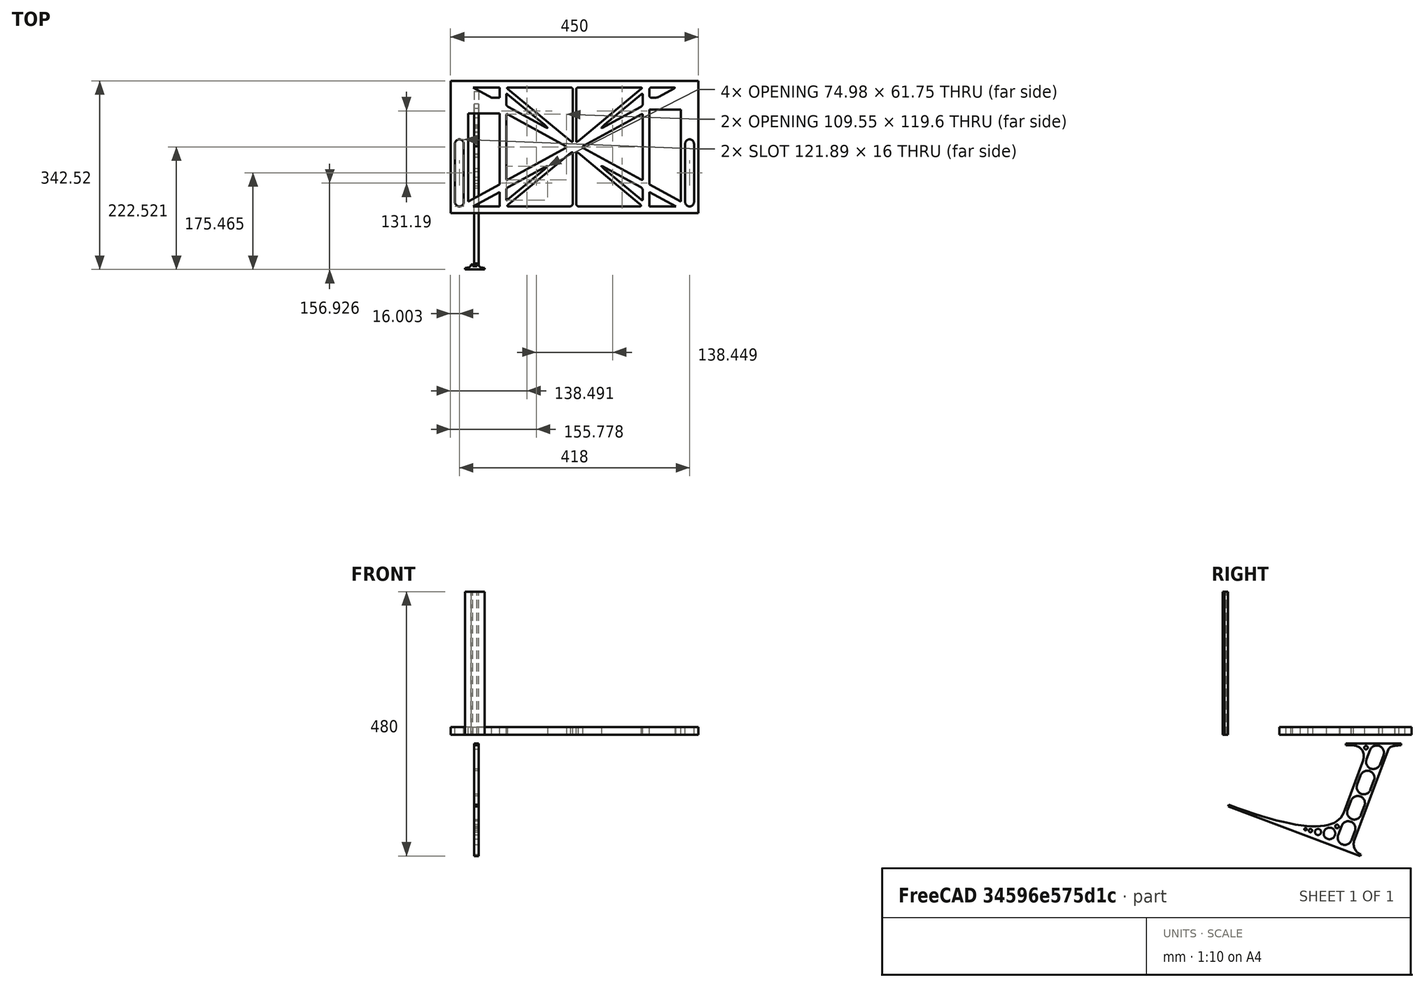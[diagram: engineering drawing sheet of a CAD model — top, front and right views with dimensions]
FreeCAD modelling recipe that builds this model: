
FCSTD DOCUMENT  (FreeCAD 0.19R0.19.2)
Label: laptopStand103
License: All rights reserved
LicenseURL: http://en.wikipedia.org/wiki/All_rights_reserved
objects: Sketcher::SketchObject×3, Part::Extrusion×3
note: 6 computed .brp shape members not serialized (recipe doc carries the construction recipe); baked Part::Feature solids carry a one-line shape summary decoded from their .brp

FEATURE [Sketcher::SketchObject] Sketch
  FullyConstrained = false
  sketch-geometry (282):
    g0: LineSegment StartX=-10.9272 StartY=-82.7794 StartZ=0 EndX=46.0728 EndY=-51.4823 EndZ=0
    g1: LineSegment StartX=366.073 StartY=-91.7794 StartZ=0 EndX=318.073 EndY=-65.424 EndZ=0
    g2: LineSegment StartX=-10.9272 StartY=77.3346 StartZ=0 EndX=-10.9272 EndY=-82.7794 EndZ=0
    g3: LineSegment StartX=375.073 StartY=-82.7896 StartZ=0 EndX=375.073 EndY=83.9235 EndZ=0
    g4: LineSegment StartX=-1.92719 StartY=-91.7794 StartZ=0 EndX=46.0728 EndY=-91.7794 EndZ=0
    g5: LineSegment StartX=318.073 StartY=83.9235 StartZ=0 EndX=318.073 EndY=-51.4823 EndZ=0
    g6: LineSegment StartX=318.073 StartY=-51.4823 StartZ=0 EndX=375.073 EndY=-82.7794 EndZ=0
    g7: LineSegment StartX=318.073 StartY=-65.424 StartZ=0 EndX=318.073 EndY=-91.7794 EndZ=0
    g8: LineSegment StartX=318.073 StartY=-91.7794 StartZ=0 EndX=366.073 EndY=-91.7794 EndZ=0
    g9: LineSegment StartX=46.0728 StartY=-65.424 StartZ=0 EndX=-1.92719 EndY=-91.7794 EndZ=0
    g10: LineSegment StartX=46.0728 StartY=-65.424 StartZ=0 EndX=46.0728 EndY=-91.7794 EndZ=0
    g11: LineSegment StartX=46.0728 StartY=77.3346 StartZ=0 EndX=46.0728 EndY=-51.4823 EndZ=0
    g12: LineSegment StartX=-42.9272 StartY=136.221 StartZ=0 EndX=-42.9272 EndY=-103.779 EndZ=0
    g13: LineSegment StartX=407.073 StartY=136.221 StartZ=0 EndX=407.073 EndY=-103.779 EndZ=0
    g14: ArcOfCircle CenterX=-26.9272 CenterY=22.1087 CenterZ=0 NormalX=0 NormalY=0 NormalZ=1 AngleXU=0 Radius=8 StartAngle=1e-16 EndAngle=3.14159
    g15: ArcOfCircle CenterX=-26.9272 CenterY=-83.7794 CenterZ=0 NormalX=0 NormalY=0 NormalZ=1 AngleXU=0 Radius=8 StartAngle=3.14159 EndAngle=6.28319
    g16: LineSegment StartX=-34.9272 StartY=22.1087 StartZ=0 EndX=-34.9272 EndY=-83.7794 EndZ=0
    g17: LineSegment StartX=-18.9272 StartY=22.1087 StartZ=0 EndX=-18.9272 EndY=-83.7794 EndZ=0
    g18: ArcOfCircle CenterX=391.073 CenterY=22.1087 CenterZ=0 NormalX=0 NormalY=0 NormalZ=1 AngleXU=0 Radius=8 StartAngle=-4.4e-15 EndAngle=3.14159
    g19: LineSegment StartX=399.073 StartY=22.1087 StartZ=0 EndX=399.073 EndY=-83.7794 EndZ=0
    g20: LineSegment StartX=383.073 StartY=22.1087 StartZ=0 EndX=383.073 EndY=-83.7794 EndZ=0
    g21: ArcOfCircle CenterX=391.073 CenterY=-83.7794 CenterZ=0 NormalX=0 NormalY=0 NormalZ=1 AngleXU=0 Radius=8 StartAngle=3.14159 EndAngle=6.28319
    g22: Circle CenterX=175.022 CenterY=27.0628 CenterZ=0 NormalX=0 NormalY=0 NormalZ=1 AngleXU=0 Radius=1
    g23: Circle CenterX=179.022 CenterY=24.8665 CenterZ=0 NormalX=0 NormalY=0 NormalZ=1 AngleXU=0 Radius=1
    g24: Circle CenterX=179.022 CenterY=27.0628 CenterZ=0 NormalX=0 NormalY=0 NormalZ=1 AngleXU=0 Radius=1
    g25: BSplineCurve PolesCount=3 KnotsCount=2 Degree=2 IsPeriodic=0
    g26: GeomPoint X=175.022 Y=27.0628 Z=0
    g27: GeomPoint X=179.022 Y=27.0628 Z=0
    g28: Circle CenterX=189.124 CenterY=27.0628 CenterZ=0 NormalX=0 NormalY=0 NormalZ=1 AngleXU=0 Radius=1
    g29: Circle CenterX=185.124 CenterY=24.8665 CenterZ=0 NormalX=0 NormalY=0 NormalZ=1 AngleXU=0 Radius=1
    g30: Circle CenterX=185.124 CenterY=27.0628 CenterZ=0 NormalX=0 NormalY=0 NormalZ=1 AngleXU=0 Radius=1
    g31: BSplineCurve PolesCount=3 KnotsCount=2 Degree=2 IsPeriodic=0
    g32: GeomPoint X=189.124 Y=27.0628 Z=0
    g33: GeomPoint X=185.124 Y=27.0628 Z=0
    g34: Circle CenterX=175.022 CenterY=5.37834 CenterZ=0 NormalX=0 NormalY=0 NormalZ=1 AngleXU=0 Radius=1
    g35: Circle CenterX=179.022 CenterY=7.57463 CenterZ=0 NormalX=0 NormalY=0 NormalZ=1 AngleXU=0 Radius=1
    g36: Circle CenterX=179.022 CenterY=5.34704 CenterZ=0 NormalX=0 NormalY=0 NormalZ=1 AngleXU=0 Radius=1
    g37: BSplineCurve PolesCount=3 KnotsCount=2 Degree=2 IsPeriodic=0
    g38: GeomPoint X=175.022 Y=5.37834 Z=0
    g39: GeomPoint X=179.022 Y=5.34704 Z=0
    g40: Circle CenterX=189.124 CenterY=5.37834 CenterZ=0 NormalX=0 NormalY=0 NormalZ=1 AngleXU=0 Radius=1
    g41: Circle CenterX=185.124 CenterY=7.57463 CenterZ=0 NormalX=0 NormalY=0 NormalZ=1 AngleXU=0 Radius=1
    g42: Circle CenterX=185.124 CenterY=5.34704 CenterZ=0 NormalX=0 NormalY=0 NormalZ=1 AngleXU=0 Radius=1
    g43: BSplineCurve PolesCount=3 KnotsCount=2 Degree=2 IsPeriodic=0
    g44: GeomPoint X=189.124 Y=5.37834 Z=0
    g45: GeomPoint X=185.124 Y=5.34704 Z=0
    g46: Circle CenterX=165.871 CenterY=18.1458 CenterZ=0 NormalX=0 NormalY=0 NormalZ=1 AngleXU=0 Radius=1
    g47: Circle CenterX=169.377 CenterY=16.2206 CenterZ=0 NormalX=0 NormalY=0 NormalZ=1 AngleXU=0 Radius=1
    g48: Circle CenterX=165.871 CenterY=14.2954 CenterZ=0 NormalX=0 NormalY=0 NormalZ=1 AngleXU=0 Radius=1
    g49: BSplineCurve PolesCount=3 KnotsCount=2 Degree=2 IsPeriodic=0
    g50: GeomPoint X=165.871 Y=18.1458 Z=0
    g51: GeomPoint X=165.871 Y=14.2954 Z=0
    g52: Circle CenterX=198.275 CenterY=18.1458 CenterZ=0 NormalX=0 NormalY=0 NormalZ=1 AngleXU=0 Radius=1
    g53: Circle CenterX=194.768 CenterY=16.2206 CenterZ=0 NormalX=0 NormalY=0 NormalZ=1 AngleXU=0 Radius=1
    g54: Circle CenterX=198.275 CenterY=14.2954 CenterZ=0 NormalX=0 NormalY=0 NormalZ=1 AngleXU=0 Radius=1
    g55: BSplineCurve PolesCount=3 KnotsCount=2 Degree=2 IsPeriodic=0
    g56: GeomPoint X=198.275 Y=18.1458 Z=0
    g57: GeomPoint X=198.275 Y=14.2954 Z=0
    g58: LineSegment StartX=407.073 StartY=-103.779 StartZ=0 EndX=-42.9272 EndY=-103.779 EndZ=0
    g59: LineSegment StartX=407.073 StartY=136.221 StartZ=0 EndX=-42.9272 EndY=136.221 EndZ=0
    g60: LineSegment StartX=46.0728 StartY=77.3346 StartZ=0 EndX=-10.9272 EndY=77.3346 EndZ=0
    g61: LineSegment StartX=46.0728 StartY=105.865 StartZ=0 EndX=31.5028 EndY=105.865 EndZ=0
    g62: LineSegment StartX=46.0728 StartY=124.221 StartZ=0 EndX=46.0728 EndY=105.865 EndZ=0
    g63: LineSegment StartX=-1.92719 StartY=124.221 StartZ=0 EndX=31.5028 EndY=105.865 EndZ=0
    g64: LineSegment StartX=46.0728 StartY=124.221 StartZ=0 EndX=-1.92719 EndY=124.221 EndZ=0
    g65: LineSegment StartX=318.073 StartY=83.9235 StartZ=0 EndX=375.073 EndY=83.9235 EndZ=0
    g66: Circle CenterX=125.607 CenterY=54.1951 CenterZ=0 NormalX=0 NormalY=0 NormalZ=1 AngleXU=0 Radius=1
    g67: Circle CenterX=139.632 CenterY=46.4944 CenterZ=0 NormalX=0 NormalY=0 NormalZ=1 AngleXU=0 Radius=1
    g68: Circle CenterX=127.326 CenterY=56.7187 CenterZ=0 NormalX=0 NormalY=0 NormalZ=1 AngleXU=0 Radius=1
    g69: BSplineCurve PolesCount=3 KnotsCount=2 Degree=2 IsPeriodic=0
    g70: GeomPoint X=125.607 Y=54.1951 Z=0
    g71: GeomPoint X=127.326 Y=56.7187 Z=0
    g72: Circle CenterX=236.821 CenterY=56.7187 CenterZ=0 NormalX=0 NormalY=0 NormalZ=1 AngleXU=0 Radius=1
    g73: Circle CenterX=224.513 CenterY=46.4944 CenterZ=0 NormalX=0 NormalY=0 NormalZ=1 AngleXU=0 Radius=1
    g74: Circle CenterX=238.538 CenterY=54.1951 CenterZ=0 NormalX=0 NormalY=0 NormalZ=1 AngleXU=0 Radius=1
    g75: BSplineCurve PolesCount=3 KnotsCount=2 Degree=2 IsPeriodic=0
    g76: GeomPoint X=236.821 Y=56.7187 Z=0
    g77: GeomPoint X=238.538 Y=54.1951 Z=0
    g78: Circle CenterX=238.538 CenterY=-21.7539 CenterZ=0 NormalX=0 NormalY=0 NormalZ=1 AngleXU=0 Radius=1
    g79: Circle CenterX=224.513 CenterY=-14.0532 CenterZ=0 NormalX=0 NormalY=0 NormalZ=1 AngleXU=0 Radius=1
    g80: Circle CenterX=236.821 CenterY=-24.2775 CenterZ=0 NormalX=0 NormalY=0 NormalZ=1 AngleXU=0 Radius=1
    g81: BSplineCurve PolesCount=3 KnotsCount=2 Degree=2 IsPeriodic=0
    g82: GeomPoint X=238.538 Y=-21.7539 Z=0
    g83: GeomPoint X=236.821 Y=-24.2775 Z=0
    g84: Circle CenterX=125.607 CenterY=-21.7539 CenterZ=0 NormalX=0 NormalY=0 NormalZ=1 AngleXU=0 Radius=1
    g85: Circle CenterX=139.632 CenterY=-14.0532 CenterZ=0 NormalX=0 NormalY=0 NormalZ=1 AngleXU=0 Radius=1
    g86: Circle CenterX=127.325 CenterY=-24.2775 CenterZ=0 NormalX=0 NormalY=0 NormalZ=1 AngleXU=0 Radius=1
    g87: BSplineCurve PolesCount=3 KnotsCount=2 Degree=2 IsPeriodic=0
    g88: GeomPoint X=125.607 Y=-21.7539 Z=0
    g89: GeomPoint X=127.325 Y=-24.2775 Z=0
    g90: Circle CenterX=302.996 CenterY=111.695 CenterZ=0 NormalX=0 NormalY=0 NormalZ=1 AngleXU=0 Radius=1
    g91: Circle CenterX=306.073 CenterY=114.251 CenterZ=0 NormalX=0 NormalY=0 NormalZ=1 AngleXU=0 Radius=1
    g92: Circle CenterX=306.073 CenterY=110.251 CenterZ=0 NormalX=0 NormalY=0 NormalZ=1 AngleXU=0 Radius=1
    g93: BSplineCurve PolesCount=3 KnotsCount=2 Degree=2 IsPeriodic=0
    g94: GeomPoint X=302.996 Y=111.695 Z=0
    g95: GeomPoint X=306.073 Y=110.251 Z=0
    g96: Circle CenterX=306.073 CenterY=95.2763 CenterZ=0 NormalX=0 NormalY=0 NormalZ=1 AngleXU=0 Radius=1
    g97: Circle CenterX=306.073 CenterY=91.2763 CenterZ=0 NormalX=0 NormalY=0 NormalZ=1 AngleXU=0 Radius=1
    g98: Circle CenterX=302.567 CenterY=89.3511 CenterZ=0 NormalX=0 NormalY=0 NormalZ=1 AngleXU=0 Radius=1
    g99: BSplineCurve PolesCount=3 KnotsCount=2 Degree=2 IsPeriodic=0
    g100: GeomPoint X=306.073 Y=95.2763 Z=0
    g101: GeomPoint X=302.567 Y=89.3511 Z=0
    g102: LineSegment StartX=306.073 StartY=110.251 StartZ=0 EndX=306.073 EndY=95.2763 EndZ=0
    g103: LineSegment StartX=302.996 StartY=111.695 StartZ=0 EndX=236.821 EndY=56.7187 EndZ=0
    g104: LineSegment StartX=238.538 StartY=54.1951 StartZ=0 EndX=302.567 EndY=89.3511 EndZ=0
    g105: Circle CenterX=61.1496 CenterY=111.695 CenterZ=0 NormalX=0 NormalY=0 NormalZ=1 AngleXU=0 Radius=1
    g106: Circle CenterX=58.0728 CenterY=114.251 CenterZ=0 NormalX=0 NormalY=0 NormalZ=1 AngleXU=0 Radius=1
    g107: Circle CenterX=58.0728 CenterY=110.251 CenterZ=0 NormalX=0 NormalY=0 NormalZ=1 AngleXU=0 Radius=1
    g108: BSplineCurve PolesCount=3 KnotsCount=2 Degree=2 IsPeriodic=0
    g109: GeomPoint X=61.1496 Y=111.695 Z=0
    g110: GeomPoint X=58.0728 Y=110.251 Z=0
    g111: Circle CenterX=61.5791 CenterY=89.3511 CenterZ=0 NormalX=0 NormalY=0 NormalZ=1 AngleXU=0 Radius=1
    g112: Circle CenterX=58.0728 CenterY=91.2763 CenterZ=0 NormalX=0 NormalY=0 NormalZ=1 AngleXU=0 Radius=1
    g113: Circle CenterX=58.0728 CenterY=95.2763 CenterZ=0 NormalX=0 NormalY=0 NormalZ=1 AngleXU=0 Radius=1
    g114: BSplineCurve PolesCount=3 KnotsCount=2 Degree=2 IsPeriodic=0
    g115: GeomPoint X=61.5791 Y=89.3511 Z=0
    g116: GeomPoint X=58.0728 Y=95.2763 Z=0
    g117: LineSegment StartX=58.0728 StartY=110.251 StartZ=0 EndX=58.0728 EndY=95.2763 EndZ=0
    g118: LineSegment StartX=61.1496 StartY=111.695 StartZ=0 EndX=127.326 EndY=56.7187 EndZ=0
    g119: LineSegment StartX=125.607 StartY=54.1951 StartZ=0 EndX=61.5791 EndY=89.3511 EndZ=0
    g120: Circle CenterX=61.5791 CenterY=-56.9099 CenterZ=0 NormalX=0 NormalY=0 NormalZ=1 AngleXU=0 Radius=1
    g121: Circle CenterX=58.0728 CenterY=-58.8351 CenterZ=0 NormalX=0 NormalY=0 NormalZ=1 AngleXU=0 Radius=1
    g122: Circle CenterX=58.0728 CenterY=-62.8351 CenterZ=0 NormalX=0 NormalY=0 NormalZ=1 AngleXU=0 Radius=1
    g123: BSplineCurve PolesCount=3 KnotsCount=2 Degree=2 IsPeriodic=0
    g124: GeomPoint X=61.5791 Y=-56.9099 Z=0
    g125: GeomPoint X=58.0728 Y=-62.8351 Z=0
    g126: Circle CenterX=58.0728 CenterY=-77.8102 CenterZ=0 NormalX=0 NormalY=0 NormalZ=1 AngleXU=0 Radius=1
    g127: Circle CenterX=58.0728 CenterY=-81.8102 CenterZ=0 NormalX=0 NormalY=0 NormalZ=1 AngleXU=0 Radius=1
    g128: Circle CenterX=61.1496 CenterY=-79.2541 CenterZ=0 NormalX=0 NormalY=0 NormalZ=1 AngleXU=0 Radius=1
    g129: BSplineCurve PolesCount=3 KnotsCount=2 Degree=2 IsPeriodic=0
    g130: GeomPoint X=58.0728 Y=-77.8102 Z=0
    g131: GeomPoint X=61.1496 Y=-79.2541 Z=0
    g132: LineSegment StartX=58.0728 StartY=-62.8351 StartZ=0 EndX=58.0728 EndY=-77.8102 EndZ=0
    g133: LineSegment StartX=61.1496 StartY=-79.2541 StartZ=0 EndX=127.325 EndY=-24.2775 EndZ=0
    g134: LineSegment StartX=125.607 StartY=-21.7539 StartZ=0 EndX=61.5791 EndY=-56.9099 EndZ=0
    g135: Circle CenterX=302.567 CenterY=-56.9099 CenterZ=0 NormalX=0 NormalY=0 NormalZ=1 AngleXU=0 Radius=1
    g136: Circle CenterX=306.073 CenterY=-58.8351 CenterZ=0 NormalX=0 NormalY=0 NormalZ=1 AngleXU=0 Radius=1
    g137: Circle CenterX=306.073 CenterY=-62.8351 CenterZ=0 NormalX=0 NormalY=0 NormalZ=1 AngleXU=0 Radius=1
    g138: BSplineCurve PolesCount=3 KnotsCount=2 Degree=2 IsPeriodic=0
    g139: GeomPoint X=302.567 Y=-56.9099 Z=0
    g140: GeomPoint X=306.073 Y=-62.8351 Z=0
    g141: Circle CenterX=302.996 CenterY=-79.2541 CenterZ=0 NormalX=0 NormalY=0 NormalZ=1 AngleXU=0 Radius=1
    g142: Circle CenterX=306.073 CenterY=-81.8102 CenterZ=0 NormalX=0 NormalY=0 NormalZ=1 AngleXU=0 Radius=1
    g143: Circle CenterX=306.073 CenterY=-77.8102 CenterZ=0 NormalX=0 NormalY=0 NormalZ=1 AngleXU=0 Radius=1
    g144: BSplineCurve PolesCount=3 KnotsCount=2 Degree=2 IsPeriodic=0
    g145: GeomPoint X=302.996 Y=-79.2541 Z=0
    g146: GeomPoint X=306.073 Y=-77.8102 Z=0
    g147: LineSegment StartX=306.073 StartY=-62.8351 StartZ=0 EndX=306.073 EndY=-77.8102 EndZ=0
    g148: LineSegment StartX=302.996 StartY=-79.2541 StartZ=0 EndX=236.821 EndY=-24.2775 EndZ=0
    g149: LineSegment StartX=238.538 StartY=-21.7539 StartZ=0 EndX=302.567 EndY=-56.9099 EndZ=0
    g150: Circle CenterX=61.6457 CenterY=-88.8112 CenterZ=0 NormalX=0 NormalY=0 NormalZ=1 AngleXU=0 Radius=1
    g151: Circle CenterX=58.0728 CenterY=-91.7794 CenterZ=0 NormalX=0 NormalY=0 NormalZ=1 AngleXU=0 Radius=1
    g152: Circle CenterX=63.9135 CenterY=-91.7794 CenterZ=0 NormalX=0 NormalY=0 NormalZ=1 AngleXU=0 Radius=1
    g153: BSplineCurve PolesCount=3 KnotsCount=2 Degree=2 IsPeriodic=0
    g154: GeomPoint X=61.6457 Y=-88.8112 Z=0
    g155: GeomPoint X=63.9135 Y=-91.7794 Z=0
    g156: Circle CenterX=179.022 CenterY=-85.8163 CenterZ=0 NormalX=0 NormalY=0 NormalZ=1 AngleXU=0 Radius=1
    g157: Circle CenterX=179.022 CenterY=-91.7794 CenterZ=0 NormalX=0 NormalY=0 NormalZ=1 AngleXU=0 Radius=1
    g158: Circle CenterX=171.895 CenterY=-91.7794 CenterZ=0 NormalX=0 NormalY=0 NormalZ=1 AngleXU=0 Radius=1
    g159: BSplineCurve PolesCount=3 KnotsCount=2 Degree=2 IsPeriodic=0
    g160: GeomPoint X=179.022 Y=-85.8163 Z=0
    g161: GeomPoint X=171.895 Y=-91.7794 Z=0
    g162: Circle CenterX=185.124 CenterY=-86.2028 CenterZ=0 NormalX=0 NormalY=0 NormalZ=1 AngleXU=0 Radius=1
    g163: Circle CenterX=185.124 CenterY=-91.7794 CenterZ=0 NormalX=0 NormalY=0 NormalZ=1 AngleXU=0 Radius=1
    g164: Circle CenterX=191.747 CenterY=-91.7794 CenterZ=0 NormalX=0 NormalY=0 NormalZ=1 AngleXU=0 Radius=1
    g165: BSplineCurve PolesCount=3 KnotsCount=2 Degree=2 IsPeriodic=0
    g166: GeomPoint X=185.124 Y=-86.2028 Z=0
    g167: GeomPoint X=191.747 Y=-91.7794 Z=0
    g168: Circle CenterX=299.888 CenterY=-86.6413 CenterZ=0 NormalX=0 NormalY=0 NormalZ=1 AngleXU=0 Radius=1
    g169: Circle CenterX=306.073 CenterY=-91.7794 CenterZ=0 NormalX=0 NormalY=0 NormalZ=1 AngleXU=0 Radius=1
    g170: Circle CenterX=298.776 CenterY=-91.7794 CenterZ=0 NormalX=0 NormalY=0 NormalZ=1 AngleXU=0 Radius=1
    g171: BSplineCurve PolesCount=3 KnotsCount=2 Degree=2 IsPeriodic=0
    g172: GeomPoint X=299.888 Y=-86.6413 Z=0
    g173: GeomPoint X=298.776 Y=-91.7794 Z=0
    g174: LineSegment StartX=189.124 StartY=5.37834 StartZ=0 EndX=299.888 EndY=-86.6413 EndZ=0
    g175: LineSegment StartX=298.776 StartY=-91.7794 StartZ=0 EndX=191.747 EndY=-91.7794 EndZ=0
    g176: LineSegment StartX=185.124 StartY=-86.2028 StartZ=0 EndX=185.124 EndY=5.34704 EndZ=0
    g177: LineSegment StartX=179.022 StartY=5.34704 StartZ=0 EndX=179.022 EndY=-85.8163 EndZ=0
    g178: LineSegment StartX=171.895 StartY=-91.7794 StartZ=0 EndX=63.9135 EndY=-91.7794 EndZ=0
    g179: LineSegment StartX=61.6457 StartY=-88.8112 StartZ=0 EndX=175.022 EndY=5.37834 EndZ=0
    g180: Circle CenterX=302.073 CenterY=124.221 CenterZ=0 NormalX=0 NormalY=0 NormalZ=1 AngleXU=0 Radius=1
    g181: Circle CenterX=306.073 CenterY=124.221 CenterZ=0 NormalX=0 NormalY=0 NormalZ=1 AngleXU=0 Radius=1
    g182: Circle CenterX=302.996 CenterY=121.665 CenterZ=0 NormalX=0 NormalY=0 NormalZ=1 AngleXU=0 Radius=1
    g183: BSplineCurve PolesCount=3 KnotsCount=2 Degree=2 IsPeriodic=0
    g184: GeomPoint X=302.073 Y=124.221 Z=0
    g185: GeomPoint X=302.996 Y=121.665 Z=0
    g186: Circle CenterX=189.124 CenterY=124.221 CenterZ=0 NormalX=0 NormalY=0 NormalZ=1 AngleXU=0 Radius=1
    g187: Circle CenterX=185.124 CenterY=124.221 CenterZ=0 NormalX=0 NormalY=0 NormalZ=1 AngleXU=0 Radius=1
    g188: Circle CenterX=185.124 CenterY=120.221 CenterZ=0 NormalX=0 NormalY=0 NormalZ=1 AngleXU=0 Radius=1
    g189: BSplineCurve PolesCount=3 KnotsCount=2 Degree=2 IsPeriodic=0
    g190: GeomPoint X=189.124 Y=124.221 Z=0
    g191: GeomPoint X=185.124 Y=120.221 Z=0
    g192: Circle CenterX=175.022 CenterY=124.221 CenterZ=0 NormalX=0 NormalY=0 NormalZ=1 AngleXU=0 Radius=1
    g193: Circle CenterX=179.022 CenterY=124.221 CenterZ=0 NormalX=0 NormalY=0 NormalZ=1 AngleXU=0 Radius=1
    g194: Circle CenterX=179.022 CenterY=120.221 CenterZ=0 NormalX=0 NormalY=0 NormalZ=1 AngleXU=0 Radius=1
    g195: BSplineCurve PolesCount=3 KnotsCount=2 Degree=2 IsPeriodic=0
    g196: GeomPoint X=175.022 Y=124.221 Z=0
    g197: GeomPoint X=179.022 Y=120.221 Z=0
    g198: Circle CenterX=62.0728 CenterY=124.221 CenterZ=0 NormalX=0 NormalY=0 NormalZ=1 AngleXU=0 Radius=1
    g199: Circle CenterX=58.0728 CenterY=124.221 CenterZ=0 NormalX=0 NormalY=0 NormalZ=1 AngleXU=0 Radius=1
    g200: Circle CenterX=61.1496 CenterY=121.665 CenterZ=0 NormalX=0 NormalY=0 NormalZ=1 AngleXU=0 Radius=1
    g201: BSplineCurve PolesCount=3 KnotsCount=2 Degree=2 IsPeriodic=0
    g202: GeomPoint X=62.0728 Y=124.221 Z=0
    g203: GeomPoint X=61.1496 Y=121.665 Z=0
    g204: LineSegment StartX=62.0728 StartY=124.221 StartZ=0 EndX=175.022 EndY=124.221 EndZ=0
    g205: LineSegment StartX=179.022 StartY=120.221 StartZ=0 EndX=179.022 EndY=27.0628 EndZ=0
    g206: LineSegment StartX=185.124 StartY=27.0628 StartZ=0 EndX=185.124 EndY=120.221 EndZ=0
    g207: LineSegment StartX=189.124 StartY=124.221 StartZ=0 EndX=302.073 EndY=124.221 EndZ=0
    g208: LineSegment StartX=302.996 StartY=121.665 StartZ=0 EndX=189.124 EndY=27.0628 EndZ=0
    g209: LineSegment StartX=175.022 StartY=27.0628 StartZ=0 EndX=61.1496 EndY=121.665 EndZ=0
    g210: Circle CenterX=61.5791 CenterY=75.4095 CenterZ=0 NormalX=0 NormalY=0 NormalZ=1 AngleXU=0 Radius=1
    g211: Circle CenterX=58.0728 CenterY=77.3346 CenterZ=0 NormalX=0 NormalY=0 NormalZ=1 AngleXU=0 Radius=1
    g212: Circle CenterX=58.0728 CenterY=73.3346 CenterZ=0 NormalX=0 NormalY=0 NormalZ=1 AngleXU=0 Radius=1
    g213: BSplineCurve PolesCount=3 KnotsCount=2 Degree=2 IsPeriodic=0
    g214: GeomPoint X=61.5791 Y=75.4095 Z=0
    g215: GeomPoint X=58.0728 Y=73.3346 Z=0
    g216: Circle CenterX=58.0728 CenterY=-40.8935 CenterZ=0 NormalX=0 NormalY=0 NormalZ=1 AngleXU=0 Radius=1
    g217: Circle CenterX=58.0728 CenterY=-44.8935 CenterZ=0 NormalX=0 NormalY=0 NormalZ=1 AngleXU=0 Radius=1
    g218: Circle CenterX=61.5791 CenterY=-42.9683 CenterZ=0 NormalX=0 NormalY=0 NormalZ=1 AngleXU=0 Radius=1
    g219: BSplineCurve PolesCount=3 KnotsCount=2 Degree=2 IsPeriodic=0
    g220: GeomPoint X=58.0728 Y=-40.8935 Z=0
    g221: GeomPoint X=61.5791 Y=-42.9683 Z=0
    g222: LineSegment StartX=61.5791 StartY=-42.9683 StartZ=0 EndX=165.871 EndY=14.2954 EndZ=0
    g223: LineSegment StartX=165.871 StartY=18.1458 StartZ=0 EndX=61.5791 EndY=75.4095 EndZ=0
    g224: LineSegment StartX=58.0728 StartY=73.3346 StartZ=0 EndX=58.0728 EndY=-40.8935 EndZ=0
    g225: Circle CenterX=302.567 CenterY=-42.9683 CenterZ=0 NormalX=0 NormalY=0 NormalZ=1 AngleXU=0 Radius=1
    g226: Circle CenterX=306.073 CenterY=-44.8935 CenterZ=0 NormalX=0 NormalY=0 NormalZ=1 AngleXU=0 Radius=1
    g227: Circle CenterX=306.073 CenterY=-40.8935 CenterZ=0 NormalX=0 NormalY=0 NormalZ=1 AngleXU=0 Radius=1
    g228: BSplineCurve PolesCount=3 KnotsCount=2 Degree=2 IsPeriodic=0
    g229: GeomPoint X=302.567 Y=-42.9683 Z=0
    g230: GeomPoint X=306.073 Y=-40.8935 Z=0
    g231: Circle CenterX=306.073 CenterY=73.3346 CenterZ=0 NormalX=0 NormalY=0 NormalZ=1 AngleXU=0 Radius=1
    g232: Circle CenterX=306.073 CenterY=77.3346 CenterZ=0 NormalX=0 NormalY=0 NormalZ=1 AngleXU=0 Radius=1
    g233: Circle CenterX=302.567 CenterY=75.4095 CenterZ=0 NormalX=0 NormalY=0 NormalZ=1 AngleXU=0 Radius=1
    g234: BSplineCurve PolesCount=3 KnotsCount=2 Degree=2 IsPeriodic=0
    g235: GeomPoint X=306.073 Y=73.3346 Z=0
    g236: GeomPoint X=302.567 Y=75.4095 Z=0
    g237: LineSegment StartX=302.567 StartY=-42.9683 StartZ=0 EndX=198.275 EndY=14.2954 EndZ=0
    g238: LineSegment StartX=198.275 StartY=18.1458 StartZ=0 EndX=302.567 EndY=75.4095 EndZ=0
    g239: LineSegment StartX=306.073 StartY=73.3346 StartZ=0 EndX=306.073 EndY=-40.8935 EndZ=0
    g240: LineSegment StartX=322.073 StartY=105.865 StartZ=0 EndX=328.643 EndY=105.865 EndZ=0
    g241: LineSegment StartX=318.073 StartY=120.221 StartZ=0 EndX=318.073 EndY=109.865 EndZ=0
    g242: LineSegment StartX=336.157 StartY=107.779 StartZ=0 EndX=362.567 EndY=122.294 EndZ=0
    g243: Circle CenterX=362.073 CenterY=124.221 CenterZ=0 NormalX=0 NormalY=0 NormalZ=1 AngleXU=0 Radius=1
    g244: Circle CenterX=366.073 CenterY=124.221 CenterZ=0 NormalX=0 NormalY=0 NormalZ=1 AngleXU=0 Radius=1
    g245: Circle CenterX=362.567 CenterY=122.294 CenterZ=0 NormalX=0 NormalY=0 NormalZ=1 AngleXU=0 Radius=1
    g246: BSplineCurve PolesCount=3 KnotsCount=2 Degree=2 IsPeriodic=0
    g247: GeomPoint X=362.073 Y=124.221 Z=0
    g248: GeomPoint X=362.567 Y=122.294 Z=0
    g249: Circle CenterX=322.073 CenterY=124.221 CenterZ=0 NormalX=0 NormalY=0 NormalZ=1 AngleXU=0 Radius=1
    g250: Circle CenterX=318.073 CenterY=124.221 CenterZ=0 NormalX=0 NormalY=0 NormalZ=1 AngleXU=0 Radius=1
    g251: Circle CenterX=318.073 CenterY=120.221 CenterZ=0 NormalX=0 NormalY=0 NormalZ=1 AngleXU=0 Radius=1
    g252: BSplineCurve PolesCount=3 KnotsCount=2 Degree=2 IsPeriodic=0
    g253: GeomPoint X=322.073 Y=124.221 Z=0
    g254: GeomPoint X=318.073 Y=120.221 Z=0
    g255: Circle CenterX=322.073 CenterY=105.865 CenterZ=0 NormalX=0 NormalY=0 NormalZ=1 AngleXU=0 Radius=1
    g256: Circle CenterX=318.073 CenterY=105.865 CenterZ=0 NormalX=0 NormalY=0 NormalZ=1 AngleXU=0 Radius=1
    g257: Circle CenterX=318.073 CenterY=109.865 CenterZ=0 NormalX=0 NormalY=0 NormalZ=1 AngleXU=0 Radius=1
    g258: BSplineCurve PolesCount=3 KnotsCount=2 Degree=2 IsPeriodic=0
    g259: GeomPoint X=322.073 Y=105.865 Z=0
    g260: GeomPoint X=318.073 Y=109.865 Z=0
    g261: Circle CenterX=336.157 CenterY=107.779 CenterZ=0 NormalX=0 NormalY=0 NormalZ=1 AngleXU=0 Radius=1
    g262: Circle CenterX=332.651 CenterY=105.853 CenterZ=0 NormalX=0 NormalY=0 NormalZ=1 AngleXU=0 Radius=1
    g263: Circle CenterX=328.643 CenterY=105.865 CenterZ=0 NormalX=0 NormalY=0 NormalZ=1 AngleXU=0 Radius=1
    g264: BSplineCurve PolesCount=3 KnotsCount=2 Degree=2 IsPeriodic=0
    g265: GeomPoint X=336.157 Y=107.779 Z=0
    g266: GeomPoint X=328.643 Y=105.865 Z=0
    g267: LineSegment StartX=322.073 StartY=124.221 StartZ=0 EndX=362.073 EndY=124.221 EndZ=0
    g268: LineSegment StartX=318.073 StartY=83.9235 StartZ=0 EndX=322.073 EndY=83.9235 EndZ=0
    g269: LineSegment StartX=318.073 StartY=83.9235 StartZ=0 EndX=318.073 EndY=79.9235 EndZ=0
    g270: LineSegment StartX=375.073 StartY=83.9235 StartZ=0 EndX=371.073 EndY=83.9235 EndZ=0
    g271: LineSegment StartX=375.073 StartY=83.9235 StartZ=0 EndX=375.073 EndY=79.9235 EndZ=0
    g272: LineSegment StartX=375.073 StartY=-82.7896 StartZ=0 EndX=375.073 EndY=-78.7896 EndZ=0
    g273: LineSegment StartX=318.073 StartY=-51.4823 StartZ=0 EndX=321.579 EndY=-53.4075 EndZ=0
    g274: LineSegment StartX=318.073 StartY=-51.4823 StartZ=0 EndX=318.073 EndY=-47.4823 EndZ=0
    g275: LineSegment StartX=375.073 StartY=-82.7896 StartZ=0 EndX=371.567 EndY=-80.8644 EndZ=0
    g276: Circle CenterX=371.567 CenterY=-80.8644 CenterZ=0 NormalX=0 NormalY=0 NormalZ=1 AngleXU=0 Radius=1
    g277: Circle CenterX=375.073 CenterY=-82.7896 CenterZ=0 NormalX=0 NormalY=0 NormalZ=1 AngleXU=0 Radius=1
    g278: Circle CenterX=375.073 CenterY=-78.7896 CenterZ=0 NormalX=0 NormalY=0 NormalZ=1 AngleXU=0 Radius=1
    g279: BSplineCurve PolesCount=3 KnotsCount=2 Degree=2 IsPeriodic=0
    g280: GeomPoint X=371.567 Y=-80.8644 Z=0
    g281: GeomPoint X=375.073 Y=-78.7896 Z=0
  constraints (485):
    c: Horizontal(g4)
    c: Coincident(g5,g6)
    c: Coincident(g7,g1)
    c: Tangent(g5,g7)
    c: Coincident(g10,g9)
    c: Coincident(g0,g11)
    c: Block(g6)
    c: Block(g3)
    c: Block(g1)
    c: Block(g7)
    c: Block(g10)
    c: Block(g9)
    c: Block(g0)
    c: Block(g2)
    c: Block(g8)
    c: Block(g4)
    c: Vertical(g12)
    c: Vertical(g13)
    c: Block(g13)
    c: Block(g12)
    c: Tangent(g14,g17) = 1.5708
    c: Tangent(g14,g16) = -1.5708
    c: Tangent(g16,g15) = -1.5708
    c: Tangent(g17,g15) = 1.5708
    c: Vertical(g16)
    c: Equal(g14,g15)
    c: Block(g17)
    c: Block(g16)
    c: Tangent(g18,g19) = 1.5708
    c: Tangent(g19,g21) = 1.5708
    c: Equal(g18,g21)
    c: Coincident(g20,g18)
    c: Coincident(g20,g21)
    c: Block(g19)
    c: Block(g20)
    c: Weight(g22) = 1
    c: Equal(g22,g23)
    c: Equal(g22,g24)
    c: InternalAlignment(g22,g25)
    c: InternalAlignment(g23,g25)
    c: InternalAlignment(g24,g25)
    c: InternalAlignment(g26,g25)
    c: InternalAlignment(g27,g25)
    c: Weight(g28) = 1
    c: Equal(g28,g29)
    c: Equal(g28,g30)
    c: InternalAlignment(g28,g31)
    c: InternalAlignment(g29,g31)
    c: InternalAlignment(g30,g31)
    c: InternalAlignment(g32,g31)
    c: InternalAlignment(g33,g31)
    c: Block(g31)
    c: Block(g25)
    c: Weight(g34) = 1
    c: Equal(g34,g35)
    c: Equal(g34,g36)
    c: InternalAlignment(g34,g37)
    c: InternalAlignment(g35,g37)
    c: InternalAlignment(g36,g37)
    c: InternalAlignment(g38,g37)
    c: InternalAlignment(g39,g37)
    c: Weight(g40) = 1
    c: Equal(g40,g41)
    c: Equal(g40,g42)
    c: InternalAlignment(g40,g43)
    c: InternalAlignment(g41,g43)
    c: InternalAlignment(g42,g43)
    c: InternalAlignment(g44,g43)
    c: InternalAlignment(g45,g43)
    c: Block(g43)
    c: Block(g37)
    c: Weight(g46) = 1
    c: Equal(g46,g47)
    c: Equal(g46,g48)
    c: InternalAlignment(g46,g49)
    c: InternalAlignment(g47,g49)
    c: InternalAlignment(g48,g49)
    c: InternalAlignment(g50,g49)
    c: InternalAlignment(g51,g49)
    c: Weight(g52) = 1
    c: Equal(g52,g53)
    c: Equal(g52,g54)
    c: InternalAlignment(g52,g55)
    c: InternalAlignment(g53,g55)
    c: InternalAlignment(g54,g55)
    c: InternalAlignment(g56,g55)
    c: InternalAlignment(g57,g55)
    c: Block(g49)
    c: Block(g55)
    c: Coincident(g58,g13)
    c: Coincident(g58,g12)
    c: Horizontal(g58)
    c: Distance(g58) = 450
    c: Coincident(g59,g13)
    c: Coincident(g59,g12)
    c: Horizontal(g59)
    c: Horizontal(g60)
    c: Coincident(g11,g60)
    c: Horizontal(g61)
    c: Vertical(g62)
    c: Block(g62)
    c: Block(g61)
    c: Block(g60)
    c: Distance(g62) = 18.3554
    c: Coincident(g64,g62)
    c: Coincident(g64,g63)
    c: Horizontal(g64)
    c: Block(g64)
    c: Block(g63)
    c: Coincident(g61,g63)
    c: Coincident(g2,g60)
    c: Coincident(g65,g5)
    c: Horizontal(g65)
    c: Block(g65)
    c: Coincident(g3,g65)
    c: Weight(g66) = 1
    c: Equal(g66,g67)
    c: Equal(g66,g68)
    c: InternalAlignment(g66,g69)
    c: InternalAlignment(g67,g69)
    c: InternalAlignment(g68,g69)
    c: InternalAlignment(g70,g69)
    c: InternalAlignment(g71,g69)
    c: Block(g69)
    c: Weight(g72) = 1
    c: Equal(g72,g73)
    c: Equal(g72,g74)
    c: InternalAlignment(g72,g75)
    c: InternalAlignment(g73,g75)
    c: InternalAlignment(g74,g75)
    c: InternalAlignment(g76,g75)
    c: InternalAlignment(g77,g75)
    c: Block(g75)
    c: Weight(g78) = 1
    c: Equal(g78,g79)
    c: Equal(g78,g80)
    c: InternalAlignment(g78,g81)
    c: InternalAlignment(g79,g81)
    c: InternalAlignment(g80,g81)
    c: InternalAlignment(g82,g81)
    c: InternalAlignment(g83,g81)
    c: Block(g81)
    c: Weight(g84) = 1
    c: Equal(g84,g85)
    c: Equal(g84,g86)
    c: InternalAlignment(g84,g87)
    c: InternalAlignment(g85,g87)
    c: InternalAlignment(g86,g87)
    c: InternalAlignment(g88,g87)
    c: InternalAlignment(g89,g87)
    c: Block(g87)
    c: Weight(g90) = 1
    c: Equal(g90,g91)
    c: Equal(g90,g92)
    c: InternalAlignment(g90,g93)
    c: InternalAlignment(g91,g93)
    c: InternalAlignment(g92,g93)
    c: InternalAlignment(g94,g93)
    c: InternalAlignment(g95,g93)
    c: Weight(g96) = 1
    c: Equal(g96,g97)
    c: Equal(g96,g98)
    c: InternalAlignment(g96,g99)
    c: InternalAlignment(g97,g99)
    c: InternalAlignment(g98,g99)
    c: InternalAlignment(g100,g99)
    c: InternalAlignment(g101,g99)
    c: Block(g93)
    c: Block(g99)
    c: Coincident(g102,g93)
    c: Coincident(g102,g99)
    c: Vertical(g102)
    c: Coincident(g103,g93)
    c: Coincident(g103,g75)
    c: Coincident(g104,g75)
    c: Coincident(g104,g99)
    c: Weight(g105) = 1
    c: Equal(g105,g106)
    c: Equal(g105,g107)
    c: InternalAlignment(g105,g108)
    c: InternalAlignment(g106,g108)
    c: InternalAlignment(g107,g108)
    c: InternalAlignment(g109,g108)
    c: InternalAlignment(g110,g108)
    c: Weight(g111) = 1
    c: Equal(g111,g112)
    c: Equal(g111,g113)
    c: InternalAlignment(g111,g114)
    c: InternalAlignment(g112,g114)
    c: InternalAlignment(g113,g114)
    c: InternalAlignment(g115,g114)
    c: InternalAlignment(g116,g114)
    c: Block(g108)
    c: Block(g114)
    c: Coincident(g117,g108)
    c: Coincident(g117,g114)
    c: Vertical(g117)
    c: Coincident(g118,g108)
    c: Coincident(g118,g69)
    c: Coincident(g119,g69)
    c: Coincident(g119,g114)
    c: Weight(g120) = 1
    c: Equal(g120,g121)
    c: Equal(g120,g122)
    c: InternalAlignment(g120,g123)
    c: InternalAlignment(g121,g123)
    c: InternalAlignment(g122,g123)
    c: InternalAlignment(g124,g123)
    c: InternalAlignment(g125,g123)
    c: Weight(g126) = 1
    c: Equal(g126,g127)
    c: Equal(g126,g128)
    c: InternalAlignment(g126,g129)
    c: InternalAlignment(g127,g129)
    c: InternalAlignment(g128,g129)
    c: InternalAlignment(g130,g129)
    c: InternalAlignment(g131,g129)
    c: Block(g123)
    c: Block(g129)
    c: Coincident(g132,g123)
    c: Coincident(g132,g129)
    c: Vertical(g132)
    c: Coincident(g133,g129)
    c: Coincident(g133,g87)
    c: Coincident(g134,g87)
    c: Coincident(g134,g123)
    c: Weight(g135) = 1
    c: Equal(g135,g136)
    c: Equal(g135,g137)
    c: InternalAlignment(g135,g138)
    c: InternalAlignment(g136,g138)
    c: InternalAlignment(g137,g138)
    c: InternalAlignment(g139,g138)
    c: InternalAlignment(g140,g138)
    c: Weight(g141) = 1
    c: Equal(g141,g142)
    c: Equal(g141,g143)
    c: InternalAlignment(g141,g144)
    c: InternalAlignment(g142,g144)
    c: InternalAlignment(g143,g144)
    c: InternalAlignment(g145,g144)
    c: InternalAlignment(g146,g144)
    c: Block(g138)
    c: Block(g144)
    c: Coincident(g147,g138)
    c: Coincident(g147,g144)
    c: Vertical(g147)
    c: Coincident(g148,g144)
    c: Coincident(g148,g81)
    c: Coincident(g149,g81)
    c: Coincident(g149,g138)
    c: Weight(g150) = 1
    c: Equal(g150,g151)
    c: Equal(g150,g152)
    c: InternalAlignment(g150,g153)
    c: InternalAlignment(g151,g153)
    c: InternalAlignment(g152,g153)
    c: InternalAlignment(g154,g153)
    c: InternalAlignment(g155,g153)
    c: Weight(g156) = 1
    c: Equal(g156,g157)
    c: Equal(g156,g158)
    c: InternalAlignment(g156,g159)
    c: InternalAlignment(g157,g159)
    c: InternalAlignment(g158,g159)
    c: InternalAlignment(g160,g159)
    c: InternalAlignment(g161,g159)
    c: Weight(g162) = 1
    c: Equal(g162,g163)
    c: Equal(g162,g164)
    c: InternalAlignment(g162,g165)
    c: InternalAlignment(g163,g165)
    c: InternalAlignment(g164,g165)
    c: InternalAlignment(g166,g165)
    c: InternalAlignment(g167,g165)
    c: Weight(g168) = 1
    c: Equal(g168,g169)
    c: Equal(g168,g170)
    c: InternalAlignment(g168,g171)
    c: InternalAlignment(g169,g171)
    c: InternalAlignment(g170,g171)
    c: InternalAlignment(g172,g171)
    c: InternalAlignment(g173,g171)
    c: Block(g171)
    c: Block(g165)
    c: Block(g159)
    c: Block(g153)
    c: Coincident(g174,g43)
    c: Coincident(g174,g171)
    c: Coincident(g175,g171)
    c: Coincident(g175,g165)
    c: Horizontal(g175)
    c: Coincident(g176,g165)
    c: Coincident(g176,g43)
    c: Vertical(g176)
    c: Coincident(g177,g37)
    c: Coincident(g177,g159)
    c: Vertical(g177)
    c: Coincident(g178,g159)
    c: Coincident(g178,g153)
    c: Horizontal(g178)
    c: Coincident(g179,g153)
    c: Coincident(g179,g37)
    c: Weight(g180) = 1
    c: Equal(g180,g181)
    c: Equal(g180,g182)
    c: InternalAlignment(g180,g183)
    c: InternalAlignment(g181,g183)
    c: InternalAlignment(g182,g183)
    c: InternalAlignment(g184,g183)
    c: InternalAlignment(g185,g183)
    c: Weight(g186) = 1
    c: Equal(g186,g187)
    c: Equal(g186,g188)
    c: InternalAlignment(g186,g189)
    c: InternalAlignment(g187,g189)
    c: InternalAlignment(g188,g189)
    c: InternalAlignment(g190,g189)
    c: InternalAlignment(g191,g189)
    c: Weight(g192) = 1
    c: Equal(g192,g193)
    c: Equal(g192,g194)
    c: InternalAlignment(g192,g195)
    c: InternalAlignment(g193,g195)
    c: InternalAlignment(g194,g195)
    c: InternalAlignment(g196,g195)
    c: InternalAlignment(g197,g195)
    c: Weight(g198) = 1
    c: Equal(g198,g199)
    c: Equal(g198,g200)
    c: InternalAlignment(g198,g201)
    c: InternalAlignment(g199,g201)
    c: InternalAlignment(g200,g201)
    c: InternalAlignment(g202,g201)
    c: InternalAlignment(g203,g201)
    c: Block(g201)
    c: Block(g195)
    c: Block(g189)
    c: Block(g183)
    c: Coincident(g204,g201)
    c: Coincident(g204,g195)
    c: Horizontal(g204)
    c: Coincident(g205,g195)
    c: Coincident(g205,g25)
    c: Vertical(g205)
    c: Coincident(g206,g31)
    c: Coincident(g206,g189)
    c: Vertical(g206)
    c: Coincident(g207,g189)
    c: Coincident(g207,g183)
    c: Horizontal(g207)
    c: Coincident(g208,g183)
    c: Coincident(g208,g31)
    c: Coincident(g209,g25)
    c: Weight(g210) = 1
    c: Equal(g210,g211)
    c: Equal(g210,g212)
    c: InternalAlignment(g210,g213)
    c: InternalAlignment(g211,g213)
    c: InternalAlignment(g212,g213)
    c: InternalAlignment(g214,g213)
    c: InternalAlignment(g215,g213)
    c: Weight(g216) = 1
    c: Equal(g216,g217)
    c: Equal(g216,g218)
    c: InternalAlignment(g216,g219)
    c: InternalAlignment(g217,g219)
    c: InternalAlignment(g218,g219)
    c: InternalAlignment(g220,g219)
    c: InternalAlignment(g221,g219)
    c: Block(g219)
    c: Block(g213)
    c: Coincident(g222,g219)
    c: Coincident(g222,g49)
    c: Coincident(g223,g49)
    c: Coincident(g223,g213)
    c: Coincident(g224,g213)
    c: Coincident(g224,g219)
    c: Vertical(g224)
    c: Weight(g225) = 1
    c: Equal(g225,g226)
    c: Equal(g225,g227)
    c: InternalAlignment(g225,g228)
    c: InternalAlignment(g226,g228)
    c: InternalAlignment(g227,g228)
    c: InternalAlignment(g229,g228)
    c: InternalAlignment(g230,g228)
    c: Weight(g231) = 1
    c: Equal(g231,g232)
    c: Equal(g231,g233)
    c: InternalAlignment(g231,g234)
    c: InternalAlignment(g232,g234)
    c: InternalAlignment(g233,g234)
    c: InternalAlignment(g235,g234)
    c: InternalAlignment(g236,g234)
    c: Block(g234)
    c: Block(g228)
    c: Coincident(g237,g228)
    c: Coincident(g237,g55)
    c: Coincident(g238,g55)
    c: Coincident(g238,g234)
    c: Coincident(g239,g234)
    c: Coincident(g239,g228)
    c: Vertical(g239)
    c: Horizontal(g240)
    c: Block(g240)
    c: Vertical(g241)
    c: Block(g241)
    c: Block(g242)
    c: Weight(g243) = 1
    c: Equal(g243,g244)
    c: Equal(g243,g245)
    c: InternalAlignment(g243,g246)
    c: InternalAlignment(g244,g246)
    c: InternalAlignment(g245,g246)
    c: InternalAlignment(g247,g246)
    c: InternalAlignment(g248,g246)
    c: Weight(g249) = 1
    c: Equal(g249,g250)
    c: Equal(g249,g251)
    c: InternalAlignment(g249,g252)
    c: InternalAlignment(g250,g252)
    c: InternalAlignment(g251,g252)
    c: InternalAlignment(g253,g252)
    c: InternalAlignment(g254,g252)
    c: Weight(g255) = 1
    c: Equal(g255,g256)
    c: Equal(g255,g257)
    c: InternalAlignment(g255,g258)
    c: InternalAlignment(g256,g258)
    c: InternalAlignment(g257,g258)
    c: InternalAlignment(g259,g258)
    c: InternalAlignment(g260,g258)
    c: Weight(g261) = 1
    c: Equal(g261,g262)
    c: Equal(g261,g263)
    c: InternalAlignment(g261,g264)
    c: InternalAlignment(g262,g264)
    c: InternalAlignment(g263,g264)
    c: InternalAlignment(g265,g264)
    c: InternalAlignment(g266,g264)
    c: Block(g246)
    c: Block(g252)
    c: Block(g258)
    c: Block(g264)
    c: Coincident(g267,g252)
    c: Coincident(g267,g246)
    c: Horizontal(g267)
    c: Block(g209)
    c: Horizontal(g268)
    c: Vertical(g269)
    c: Horizontal(g270)
    c: Vertical(g271)
    c: Vertical(g272)
    c: Vertical(g274)
    c: Parallel(g6,g273)
    c: Distance(g272) = 4
    c: Distance(g273) = 4
    c: Distance(g274) = 4
    c: Distance(g269) = 4
    c: Distance(g268) = 4
    c: Distance(g271) = 4
    c: Distance(g270) = 4
    c: Coincident(g271,g3)
    c: Coincident(g270,g3)
    c: Coincident(g268,g5)
    c: Coincident(g269,g5)
    c: Coincident(g273,g5)
    c: Coincident(g274,g5)
    c: Coincident(g272,g3)
    c: Distance(g3) = 166.713
    c: Coincident(g275,g3)
    c: Distance(g275) = 4
    c: Parallel(g6,g275)
    c: Coincident(g279,g275)
    c: Weight(g276) = 1
    c: Equal(g276,g277)
    c: Coincident(g277,g3)
    c: Equal(g276,g278)
    c: Coincident(g279,g272)
    c: InternalAlignment(g276,g279)
    c: InternalAlignment(g277,g279)
    c: InternalAlignment(g278,g279)
    c: InternalAlignment(g280,g279)
    c: InternalAlignment(g281,g279)
FEATURE [Sketcher::SketchObject] Sketch001
  FullyConstrained = true
  MapMode = 4
  Placement = pos=(0,0,0) rot=(0.57735,0.57735,0.57735;2.0944rad)
  Support = -> [Sketch]
  sketch-geometry (46):
    g0: BSplineCurve PolesCount=3 KnotsCount=2 Degree=2 IsPeriodic=0
    g1: ArcOfCircle CenterX=73.1223 CenterY=-32.291 CenterZ=0 NormalX=0 NormalY=0 NormalZ=1 AngleXU=0 Radius=13 StartAngle=5.92268 EndAngle=9.06428
    g2: ArcOfCircle CenterX=66.7816 CenterY=-49.1439 CenterZ=0 NormalX=0 NormalY=0 NormalZ=1 AngleXU=0 Radius=13 StartAngle=2.78068 EndAngle=5.92131
    g3: ArcOfCircle CenterX=55.9263 CenterY=-78.1807 CenterZ=0 NormalX=0 NormalY=0 NormalZ=1 AngleXU=0 Radius=13 StartAngle=5.92268 EndAngle=9.06428
    g4: ArcOfCircle CenterX=49.5884 CenterY=-95.0342 CenterZ=0 NormalX=0 NormalY=0 NormalZ=1 AngleXU=0 Radius=13 StartAngle=2.78068 EndAngle=5.92131
    g5: ArcOfCircle CenterX=38.7206 CenterY=-124.067 CenterZ=0 NormalX=0 NormalY=0 NormalZ=1 AngleXU=0 Radius=13 StartAngle=5.92268 EndAngle=9.06428
    g6: ArcOfCircle CenterX=32.3875 CenterY=-140.92 CenterZ=0 NormalX=0 NormalY=0 NormalZ=1 AngleXU=0 Radius=13 StartAngle=2.78068 EndAngle=5.92131
    g7: ArcOfCircle CenterX=21.4715 CenterY=-169.934 CenterZ=0 NormalX=0 NormalY=0 NormalZ=1 AngleXU=0 Radius=13 StartAngle=5.92268 EndAngle=9.06428
    g8: ArcOfCircle CenterX=15.1336 CenterY=-186.787 CenterZ=0 NormalX=0 NormalY=0 NormalZ=1 AngleXU=0 Radius=13 StartAngle=2.78068 EndAngle=5.92131
    g9-g12: Circle x4 (B-spline internal-alignment scaffolding for g13; pole/knot coordinates omitted)
    g13: BSplineCurve PolesCount=4 KnotsCount=2 Degree=3 IsPeriodic=0
    g14: GeomPoint X=28.8094 Y=-19.0875 Z=0
    g15: GeomPoint X=47.0443 Y=-50.4712 Z=0
    g16: Circle CenterX=53.5586 CenterY=-23.2695 CenterZ=0 NormalX=0 NormalY=0 NormalZ=1 AngleXU=0 Radius=3.24518
    g17: Circle CenterX=-195.441 CenterY=-127.082 CenterZ=0 NormalX=0 NormalY=0 NormalZ=1 AngleXU=0 Radius=1
    g18: Circle CenterX=-8.24091 CenterY=-197.481 CenterZ=0 NormalX=0 NormalY=0 NormalZ=1 AngleXU=0 Radius=1
    g19: Circle CenterX=12.8789 CenterY=-141.321 CenterZ=0 NormalX=0 NormalY=0 NormalZ=1 AngleXU=0 Radius=1
    g20: BSplineCurve PolesCount=3 KnotsCount=2 Degree=2 IsPeriodic=0
    g21: GeomPoint X=-195.441 Y=-127.082 Z=0
    g22: GeomPoint X=12.8789 Y=-141.321 Z=0
    g23: Circle CenterX=-12.8016 CenterY=-179.036 CenterZ=0 NormalX=0 NormalY=0 NormalZ=1 AngleXU=0 Radius=10.5072
    g24: Circle CenterX=0.933922 CenterY=-166.43 CenterZ=0 NormalX=0 NormalY=0 NormalZ=1 AngleXU=0 Radius=3.26661
    g25: Circle CenterX=-33.5518 CenterY=-176.44 CenterZ=0 NormalX=0 NormalY=0 NormalZ=1 AngleXU=0 Radius=5.64388
    g26: Circle CenterX=-47.2366 CenterY=-173.859 CenterZ=0 NormalX=0 NormalY=0 NormalZ=1 AngleXU=0 Radius=3.01653
    g27: Circle CenterX=-56.2595 CenterY=-171.456 CenterZ=0 NormalX=0 NormalY=0 NormalZ=1 AngleXU=0 Radius=2.12826
    g28: ArcOfCircle CenterX=51.2151 CenterY=-198.473 CenterZ=0 NormalX=0 NormalY=0 NormalZ=1 AngleXU=0 Radius=20 StartAngle=2.78189 EndAngle=4.35269
    g29: LineSegment StartX=32.4951 StartY=-191.433 StartZ=0 EndX=94.6578 EndY=-26.1352 EndZ=0
    g30: LineSegment StartX=43.1192 StartY=-220.001 StartZ=0 EndX=-196.497 EndY=-129.89 EndZ=0
    g31: LineSegment StartX=43.1192 StartY=-220.001 StartZ=0 EndX=44.1752 EndY=-217.193 EndZ=0
    g32: LineSegment StartX=117.223 StartY=-19.0875 StartZ=0 EndX=117.223 EndY=-16.0875 EndZ=0
    g33: LineSegment StartX=117.223 StartY=-16.0875 StartZ=0 EndX=17.2232 EndY=-16.0875 EndZ=0
    g34: LineSegment StartX=17.2232 StartY=-16.0875 StartZ=0 EndX=17.2232 EndY=-19.0875 EndZ=0
    g35: LineSegment StartX=28.8094 StartY=-19.0875 StartZ=0 EndX=17.2232 EndY=-19.0875 EndZ=0
    g36: LineSegment StartX=47.0443 StartY=-50.4712 StartZ=0 EndX=12.8789 EndY=-141.321 EndZ=0
    g37: LineSegment StartX=-195.441 StartY=-127.082 StartZ=0 EndX=-196.497 EndY=-129.89 EndZ=0
    g38: LineSegment StartX=85.2866 StartY=-36.8766 StartZ=0 EndX=78.9396 EndY=-53.7463 EndZ=0
    g39: LineSegment StartX=60.9579 StartY=-27.7053 StartZ=0 EndX=54.6191 EndY=-44.5532 EndZ=0
    g40: LineSegment StartX=68.0907 StartY=-82.7664 StartZ=0 EndX=61.7465 EndY=-99.6365 EndZ=0
    g41: LineSegment StartX=43.7619 StartY=-73.595 StartZ=0 EndX=37.426 EndY=-90.4435 EndZ=0
    g42: LineSegment StartX=50.885 StartY=-128.652 StartZ=0 EndX=44.5456 EndY=-145.522 EndZ=0
    g43: LineSegment StartX=26.5562 StartY=-119.481 StartZ=0 EndX=20.2251 EndY=-136.329 EndZ=0
    g44: LineSegment StartX=9.3071 StartY=-165.349 StartZ=0 EndX=2.97115 EndY=-182.197 EndZ=0
    g45: LineSegment StartX=33.6358 StartY=-174.52 StartZ=0 EndX=27.2917 EndY=-191.39 EndZ=0
  constraints (71):
    c: Block(g0)
    c: Block(g1)
    c: Block(g2)
    c: Block(g4)
    c: Block(g3)
    c: Block(g6)
    c: Block(g5)
    c: Block(g8)
    c: Block(g7)
    c: Weight(g9) = 1
    c: Equal(g9,g10)
    c: Equal(g9,g11)
    c: Equal(g9,g12)
    c: InternalAlignment(g9-g12 -> g13) x4
    c: InternalAlignment(g14,g13)
    c: InternalAlignment(g15,g13)
    c: Block(g16)
    c: Weight(g17) = 1
    c: Equal(g17,g18)
    c: Equal(g17,g19)
    c: InternalAlignment(g17,g20)
    c: InternalAlignment(g18,g20)
    c: InternalAlignment(g19,g20)
    c: InternalAlignment(g21,g20)
    c: InternalAlignment(g22,g20)
    c: Block(g20)
    c: Block(g23)
    c: Block(g24)
    c: Block(g25)
    c: Block(g26)
    c: Block(g27)
    c: Block(g28)
    c: Coincident(g29,g28)
    c: Coincident(g29,g0)
    c: Block(g13)
    c: Coincident(g31,g30)
    c: Coincident(g31,g28)
    c: Block(g31)
    c: Coincident(g32,g0)
    c: Vertical(g32)
    c: Coincident(g33,g32)
    c: Horizontal(g33)
    c: Coincident(g34,g33)
    c: Vertical(g34)
    c: Block(g33)
    c: Coincident(g35,g13)
    c: Coincident(g35,g34)
    c: Horizontal(g35)
    c: Coincident(g36,g13)
    c: Coincident(g36,g20)
    c: Coincident(g37,g20)
    c: Coincident(g37,g30)
    c: Block(g30)
    c: Coincident(g38,g1)
    c: Coincident(g38,g2)
    c: Coincident(g39,g1)
    c: Coincident(g39,g2)
    c: Coincident(g40,g3)
    c: Coincident(g40,g4)
    c: Coincident(g41,g3)
    c: Coincident(g41,g4)
    c: Coincident(g42,g5)
    c: Coincident(g42,g6)
    c: Coincident(g43,g5)
    c: Coincident(g43,g6)
    c: Coincident(g44,g7)
    c: Coincident(g44,g8)
    c: Coincident(g45,g7)
    c: Coincident(g45,g8)
    c: Distance(g30) = 256
    c: Distance(g33) = 100
FEATURE [Part::Extrusion] Extrude002
  Base = -> Sketch001
  Dir = (1,0,0)
  DirMode = 2
  FaceMakerClass = Part::FaceMakerBullseye
  LengthFwd = 8
  LengthRev = 0
  Solid = true
  Symmetric = false
FEATURE [Sketcher::SketchObject] Sketch002
  FullyConstrained = true
  sketch-geometry (20):
    g0: LineSegment StartX=-2.77179 StartY=-200.304 StartZ=0 EndX=5.22821 EndY=-200.304 EndZ=0
    g1: LineSegment StartX=5.22821 StartY=-200.304 StartZ=0 EndX=5.22821 EndY=-197.304 EndZ=0
    g2: LineSegment StartX=-2.77179 StartY=-200.304 StartZ=0 EndX=-2.77179 EndY=-197.304 EndZ=0
    g3: LineSegment StartX=5.22821 StartY=-197.304 StartZ=0 EndX=8.22821 EndY=-197.304 EndZ=0
    g4: LineSegment StartX=-2.77179 StartY=-197.304 StartZ=0 EndX=-5.77179 EndY=-197.304 EndZ=0
    g5: LineSegment StartX=19.2282 StartY=-203.304 StartZ=0 EndX=19.2282 EndY=-206.304 EndZ=0
    g6: LineSegment StartX=-16.7718 StartY=-203.304 StartZ=0 EndX=-16.7718 EndY=-206.304 EndZ=0
    g7: LineSegment StartX=-16.7718 StartY=-206.304 StartZ=0 EndX=19.2282 EndY=-206.304 EndZ=0
    g8: Circle CenterX=-16.7718 CenterY=-203.304 CenterZ=0 NormalX=0 NormalY=0 NormalZ=1 AngleXU=0 Radius=1
    g9: Circle CenterX=-5.77179 CenterY=-203.304 CenterZ=0 NormalX=0 NormalY=0 NormalZ=1 AngleXU=0 Radius=1
    g10: Circle CenterX=-5.77179 CenterY=-197.304 CenterZ=0 NormalX=0 NormalY=0 NormalZ=1 AngleXU=0 Radius=1
    g11: BSplineCurve PolesCount=3 KnotsCount=2 Degree=2 IsPeriodic=0
    g12: GeomPoint X=-16.7718 Y=-203.304 Z=0
    g13: GeomPoint X=-5.77179 Y=-197.304 Z=0
    g14: Circle CenterX=19.2282 CenterY=-203.304 CenterZ=0 NormalX=0 NormalY=0 NormalZ=1 AngleXU=0 Radius=1
    g15: Circle CenterX=8.22821 CenterY=-203.304 CenterZ=0 NormalX=0 NormalY=0 NormalZ=1 AngleXU=0 Radius=1
    g16: Circle CenterX=8.22821 CenterY=-197.304 CenterZ=0 NormalX=0 NormalY=0 NormalZ=1 AngleXU=0 Radius=1
    g17: BSplineCurve PolesCount=3 KnotsCount=2 Degree=2 IsPeriodic=0
    g18: GeomPoint X=19.2282 Y=-203.304 Z=0
    g19: GeomPoint X=8.22821 Y=-197.304 Z=0
  constraints (41):
    c: Horizontal(g0)
    c: Distance(g0) = 8
    c: Coincident(g1,g0)
    c: Vertical(g1)
    c: Distance(g1) = 3
    c: Coincident(g2,g0)
    c: Vertical(g2)
    c: Distance(g2) = 3
    c: Coincident(g3,g1)
    c: Horizontal(g3)
    c: Distance(g3) = 3
    c: Coincident(g4,g2)
    c: Horizontal(g4)
    c: Distance(g4) = 3
    c: Vertical(g5)
    c: Vertical(g6)
    c: Coincident(g7,g6)
    c: Coincident(g7,g5)
    c: Weight(g8) = 1
    c: Equal(g8,g9)
    c: Equal(g8,g10)
    c: Coincident(g11,g4)
    c: InternalAlignment(g8,g11)
    c: InternalAlignment(g9,g11)
    c: InternalAlignment(g10,g11)
    c: InternalAlignment(g12,g11)
    c: InternalAlignment(g13,g11)
    c: Coincident(g17,g5)
    c: Weight(g14) = 1
    c: Equal(g14,g15)
    c: Equal(g14,g16)
    c: Coincident(g17,g3)
    c: InternalAlignment(g14,g17)
    c: InternalAlignment(g15,g17)
    c: InternalAlignment(g16,g17)
    c: InternalAlignment(g18,g17)
    c: InternalAlignment(g19,g17)
    c: Block(g7)
    c: Block(g17)
    c: Block(g11)
    c: Block(g6)
FEATURE [Part::Extrusion] Extrude003
  Base = -> Sketch002
  Dir = (0,0,1)
  DirMode = 2
  FaceMakerClass = Part::FaceMakerBullseye
  LengthFwd = 260
  LengthRev = 0
  Solid = true
  Symmetric = false
FEATURE [Part::Extrusion] Extrude
  Base = -> Sketch
  Dir = (0,0,1)
  DirMode = 2
  FaceMakerClass = Part::FaceMakerBullseye
  LengthFwd = 14
  LengthRev = 0
  Solid = true
  Symmetric = false
